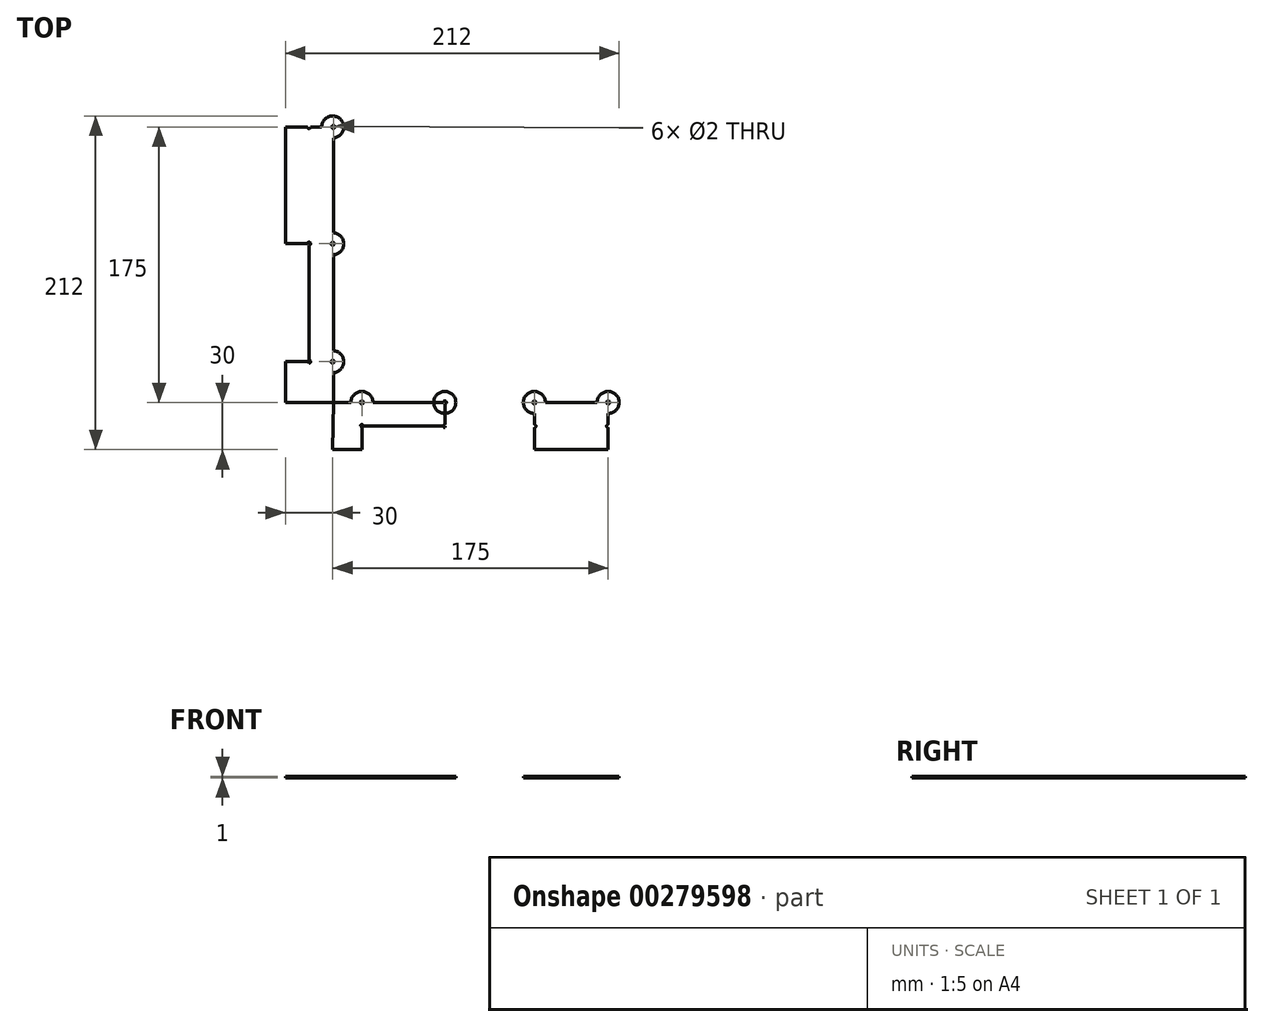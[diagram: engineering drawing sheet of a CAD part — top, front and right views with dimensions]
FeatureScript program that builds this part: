
annotation { "Feature Type Name" : "Feature", "Feature Type Description" : "" }
export const myFeature = defineFeature(function(context is Context, id is Id, definition is map)
    precondition{}
    {
        {
            var Q0;
            Q0=qCreatedBy(makeId("Top.planeOp"),FACE);
            var sketch = newSketch(context, id + "F0", { "sketchPlane" : qUnion([Q0])});
            skLineSegment(sketch, "E0", {"start": v(0, 0) * mm, "end": v(18.55, 0) * mm, "construction": true});
            skCircle(sketch, "E1", {"center": v(18.55, 0) * mm, "radius": 7 * mm});
            skLineSegment(sketch, "E2", {"start": v(0, 0) * mm, "end": v(71.22, 0) * mm, "construction": true});
            skCircle(sketch, "E3", {"center": v(71.22, 0) * mm, "radius": 7 * mm});
            skLineSegment(sketch, "E4", {"start": v(0, 0) * mm, "end": v(128.1, 0) * mm, "construction": true});
            skCircle(sketch, "E5", {"center": v(128.1, 0) * mm, "radius": 7 * mm});
            skLineSegment(sketch, "E6", {"start": v(0, 0) * mm, "end": v(175, 0) * mm, "construction": true});
            skCircle(sketch, "E7", {"center": v(175, 0) * mm, "radius": 7 * mm});
            skLineSegment(sketch, "E8", {"start": v(0, 0) * mm, "end": v(0, 25.9) * mm, "construction": true});
            skLineSegment(sketch, "E9", {"start": v(0, 0) * mm, "end": v(0, 100.8) * mm, "construction": true});
            skLineSegment(sketch, "E10", {"start": v(0, 0) * mm, "end": v(0, 175) * mm, "construction": true});
            skCircle(sketch, "E11", {"center": v(0, 25.9) * mm, "radius": 7 * mm});
            skCircle(sketch, "E12", {"center": v(0, 100.8) * mm, "radius": 7 * mm});
            skCircle(sketch, "E13", {"center": v(0, 175) * mm, "radius": 7 * mm});
            skLineSegment(sketch, "E14.0", {"start": v(0, -15) * mm, "end": v(175, -15) * mm});
            skLineSegment(sketch, "E15.0", {"start": v(0, -30) * mm, "end": v(175, -30) * mm});
            skLineSegment(sketch, "E16.0", {"start": v(0.46, 0) * mm, "end": v(0.46, 175) * mm});
            skLineSegment(sketch, "E17.0", {"start": v(-15, 0) * mm, "end": v(-15, 175) * mm});
            skLineSegment(sketch, "E18.0", {"start": v(-30, 0) * mm, "end": v(-30, 175) * mm});
            skLineSegment(sketch, "E19", {"start": v(18.55, 0) * mm, "end": v(18.55, -30) * mm});
            skLineSegment(sketch, "E20", {"start": v(71.22, 0) * mm, "end": v(71.22, -30) * mm});
            skLineSegment(sketch, "E21", {"start": v(128.1, 0) * mm, "end": v(128.1, -30) * mm});
            skLineSegment(sketch, "E22", {"start": v(175, 0) * mm, "end": v(175, -30) * mm});
            skLineSegment(sketch, "E23", {"start": v(0.46, 175) * mm, "end": v(-30, 175) * mm});
            skLineSegment(sketch, "E24", {"start": v(0, 100.8) * mm, "end": v(-30, 100.8) * mm});
            skPoint(sketch, "E24.endSnap0", {"position": v(-30, 87.5) * mm});
            skLineSegment(sketch, "E25", {"start": v(0, 25.9) * mm, "end": v(-30, 25.9) * mm});
            skCircle(sketch, "E26", {"center": v(-15, 175) * mm, "radius": 1 * mm});
            skCircle(sketch, "E27", {"center": v(-15, 100.8) * mm, "radius": 1 * mm});
            skCircle(sketch, "E28", {"center": v(-15, 25.9) * mm, "radius": 1 * mm});
            skCircle(sketch, "E29", {"center": v(18.55, -15) * mm, "radius": 1 * mm});
            skCircle(sketch, "E30", {"center": v(71.22, -15) * mm, "radius": 1 * mm});
            skCircle(sketch, "E31", {"center": v(128.1, -15) * mm, "radius": 1 * mm});
            skCircle(sketch, "E32", {"center": v(175, -15) * mm, "radius": 1 * mm});
            skLineSegment(sketch, "E33", {"start": v(0.46, 0) * mm, "end": v(0, -30) * mm});
            skLineSegment(sketch, "E34", {"start": v(0.46, 0) * mm, "end": v(-30, 0) * mm});
            skLineSegment(sketch, "E35", {"start": v(0.46, 0) * mm, "end": v(175, 0) * mm});
            skCircle(sketch, "E36", {"center": v(0.46, 175) * mm, "radius": 1 * mm});
            skCircle(sketch, "E37", {"center": v(0, 100.8) * mm, "radius": 1 * mm});
            skCircle(sketch, "E38", {"center": v(0, 25.9) * mm, "radius": 1 * mm});
            skCircle(sketch, "E39", {"center": v(18.55, 0) * mm, "radius": 1 * mm});
            skCircle(sketch, "E40", {"center": v(71.22, 0) * mm, "radius": 1 * mm});
            skCircle(sketch, "E41", {"center": v(128.1, 0) * mm, "radius": 1 * mm});
            skCircle(sketch, "E42", {"center": v(175, 0) * mm, "radius": 1 * mm});
            skSolve(sketch);
        }
        {
            var Q0;
            {var subQ0=sQuery(id+"F0.wireOp",EDGE,"E22");var subQ1=sQuery(id+"F0.wireOp",EDGE,"E7");var subQ2=makeQuery(id+"F0.imprint","INTERSECT",VERTEX,{"derivedFrom":[subQ1,subQ0]});Q0=makeQuery(id+"F0.imprint","IMPRINT",FACE,{"disambiguationData":[TD([[makeQuery(id+"F0.imprint","IMPRINT",EDGE,{"disambiguationData":[TD([[subQ2,-1.0]])],"derivedFrom":subQ1}),1.0]])]});}
            var Q1;
            {var subQ0=sQuery(id+"F0.wireOp",EDGE,"E16.0");var subQ1=sQuery(id+"F0.wireOp",EDGE,"E13");var subQ2=makeQuery(id+"F0.imprint","INTERSECT",VERTEX,{"derivedFrom":[subQ1,subQ0]});Q1=makeQuery(id+"F0.imprint","IMPRINT",FACE,{"disambiguationData":[TD([[makeQuery(id+"F0.imprint","IMPRINT",EDGE,{"disambiguationData":[TD([[subQ2,-1.0]])],"derivedFrom":subQ1}),1.0]])]});}
            var Q2;
            {var subQ0=sQuery(id+"F0.wireOp",EDGE,"E35");var subQ1=sQuery(id+"F0.wireOp",EDGE,"E1");var subQ2=makeQuery(id+"F0.imprint","INTERSECT",VERTEX,{"disambiguationData":[OD(0.0)],"derivedFrom":[subQ1,subQ0]});Q2=makeQuery(id+"F0.imprint","IMPRINT",FACE,{"disambiguationData":[TD([[makeQuery(id+"F0.imprint","IMPRINT",EDGE,{"disambiguationData":[TD([[subQ2,1.0]])],"derivedFrom":subQ1}),1.0]])]});}
            var Q3;
            {var subQ0=sQuery(id+"F0.wireOp",EDGE,"E35");var subQ1=sQuery(id+"F0.wireOp",EDGE,"E3");var subQ2=makeQuery(id+"F0.imprint","INTERSECT",VERTEX,{"disambiguationData":[OD(0.0)],"derivedFrom":[subQ1,subQ0]});Q3=makeQuery(id+"F0.imprint","IMPRINT",FACE,{"disambiguationData":[TD([[makeQuery(id+"F0.imprint","IMPRINT",EDGE,{"disambiguationData":[TD([[subQ2,1.0]])],"derivedFrom":subQ1}),1.0]])]});}
            var Q4;
            {var subQ0=sQuery(id+"F0.wireOp",EDGE,"E35");var subQ1=sQuery(id+"F0.wireOp",EDGE,"E5");var subQ2=makeQuery(id+"F0.imprint","INTERSECT",VERTEX,{"disambiguationData":[OD(0.0)],"derivedFrom":[subQ1,subQ0]});Q4=makeQuery(id+"F0.imprint","IMPRINT",FACE,{"disambiguationData":[TD([[makeQuery(id+"F0.imprint","IMPRINT",EDGE,{"disambiguationData":[TD([[subQ2,1.0]])],"derivedFrom":subQ1}),1.0]])]});}
            var Q5;
            {var subQ0=sQuery(id+"F0.wireOp",EDGE,"E22");var subQ1=sQuery(id+"F0.wireOp",EDGE,"E7");var subQ2=makeQuery(id+"F0.imprint","INTERSECT",VERTEX,{"derivedFrom":[subQ1,subQ0]});Q5=makeQuery(id+"F0.imprint","IMPRINT",FACE,{"disambiguationData":[TD([[makeQuery(id+"F0.imprint","IMPRINT",EDGE,{"disambiguationData":[TD([[subQ2,1.0]])],"derivedFrom":subQ1}),1.0]])]});}
            var Q6;
            {var subQ0=sQuery(id+"F0.wireOp",EDGE,"E16.0");var subQ1=sQuery(id+"F0.wireOp",EDGE,"E11");var subQ2=makeQuery(id+"F0.imprint","INTERSECT",VERTEX,{"disambiguationData":[OD(0.0)],"derivedFrom":[subQ1,subQ0]});Q6=makeQuery(id+"F0.imprint","IMPRINT",FACE,{"disambiguationData":[TD([[makeQuery(id+"F0.imprint","IMPRINT",EDGE,{"disambiguationData":[TD([[subQ2,1.0]])],"derivedFrom":subQ1}),1.0]])]});}
            var Q7;
            {var subQ0=sQuery(id+"F0.wireOp",EDGE,"E16.0");var subQ1=sQuery(id+"F0.wireOp",EDGE,"E12");var subQ2=makeQuery(id+"F0.imprint","INTERSECT",VERTEX,{"disambiguationData":[OD(0.0)],"derivedFrom":[subQ1,subQ0]});Q7=makeQuery(id+"F0.imprint","IMPRINT",FACE,{"disambiguationData":[TD([[makeQuery(id+"F0.imprint","IMPRINT",EDGE,{"disambiguationData":[TD([[subQ2,1.0]])],"derivedFrom":subQ1}),1.0]])]});}
            var Q8;
            {var subQ0=sQuery(id+"F0.wireOp",EDGE,"E16.0");var subQ1=sQuery(id+"F0.wireOp",EDGE,"E13");var subQ2=makeQuery(id+"F0.imprint","INTERSECT",VERTEX,{"derivedFrom":[subQ1,subQ0]});Q8=makeQuery(id+"F0.imprint","IMPRINT",FACE,{"disambiguationData":[TD([[makeQuery(id+"F0.imprint","IMPRINT",EDGE,{"disambiguationData":[TD([[subQ2,1.0]])],"derivedFrom":subQ1}),1.0]])]});}
            var Q9;
            {var subQ1=sQuery(id+"F0.wireOp",EDGE,"E14.0");var subQ7=sQuery(id+"F0.wireOp",EDGE,"E33");var subQ9=makeQuery(id+"F0.imprint","INTERSECT",VERTEX,{"derivedFrom":[subQ1,subQ7]});Q9=makeQuery(id+"F0.imprint","IMPRINT",FACE,{"disambiguationData":[TD([[makeQuery(id+"F0.imprint","IMPRINT",EDGE,{"disambiguationData":[TD([[subQ9,-1.0]])],"derivedFrom":subQ1}),-1.0]])]});}
            var Q10;
            {var subQ5=sQuery(id+"F0.wireOp",EDGE,"E34");var subQ7=sQuery(id+"F0.wireOp",EDGE,"E17.0");var subQ9=makeQuery(id+"F0.imprint","INTERSECT",VERTEX,{"derivedFrom":[subQ7,subQ5]});Q10=makeQuery(id+"F0.imprint","IMPRINT",FACE,{"disambiguationData":[TD([[makeQuery(id+"F0.imprint","IMPRINT",EDGE,{"disambiguationData":[TD([[subQ9,-1.0]])],"derivedFrom":subQ7}),1.0]])]});}
            var Q11;
            {var subQ5=sQuery(id+"F0.wireOp",EDGE,"E35");var subQ6=sQuery(id+"F0.wireOp",EDGE,"E1");var subQ7=makeQuery(id+"F0.imprint","INTERSECT",VERTEX,{"disambiguationData":[OD(0.0)],"derivedFrom":[subQ6,subQ5]});Q11=makeQuery(id+"F0.imprint","IMPRINT",FACE,{"disambiguationData":[TD([[makeQuery(id+"F0.imprint","IMPRINT",EDGE,{"disambiguationData":[TD([[subQ7,-1.0]])],"derivedFrom":subQ6}),-1.0]])]});}
            var Q12;
            {var subQ0=sQuery(id+"F0.wireOp",EDGE,"E35");var subQ1=sQuery(id+"F0.wireOp",EDGE,"E1");var subQ2=makeQuery(id+"F0.imprint","INTERSECT",VERTEX,{"disambiguationData":[OD(0.0)],"derivedFrom":[subQ1,subQ0]});Q12=makeQuery(id+"F0.imprint","IMPRINT",FACE,{"disambiguationData":[TD([[makeQuery(id+"F0.imprint","IMPRINT",EDGE,{"disambiguationData":[TD([[subQ2,-1.0]])],"derivedFrom":subQ1}),1.0]])]});}
            var Q13;
            {var subQ0=sQuery(id+"F0.wireOp",EDGE,"E35");var subQ1=sQuery(id+"F0.wireOp",EDGE,"E1");var subQ2=makeQuery(id+"F0.imprint","INTERSECT",VERTEX,{"disambiguationData":[OD(1.0)],"derivedFrom":[subQ1,subQ0]});Q13=makeQuery(id+"F0.imprint","IMPRINT",FACE,{"disambiguationData":[TD([[makeQuery(id+"F0.imprint","IMPRINT",EDGE,{"disambiguationData":[TD([[subQ2,1.0]])],"derivedFrom":subQ1}),1.0]])]});}
            var Q14;
            {var subQ0=sQuery(id+"F0.wireOp",EDGE,"E35");var subQ1=sQuery(id+"F0.wireOp",EDGE,"E3");var subQ2=makeQuery(id+"F0.imprint","INTERSECT",VERTEX,{"disambiguationData":[OD(0.0)],"derivedFrom":[subQ1,subQ0]});Q14=makeQuery(id+"F0.imprint","IMPRINT",FACE,{"disambiguationData":[TD([[makeQuery(id+"F0.imprint","IMPRINT",EDGE,{"disambiguationData":[TD([[subQ2,-1.0]])],"derivedFrom":subQ1}),1.0]])]});}
            var Q15;
            {var subQ0=sQuery(id+"F0.wireOp",EDGE,"E35");var subQ1=sQuery(id+"F0.wireOp",EDGE,"E3");var subQ2=makeQuery(id+"F0.imprint","INTERSECT",VERTEX,{"disambiguationData":[OD(1.0)],"derivedFrom":[subQ1,subQ0]});Q15=makeQuery(id+"F0.imprint","IMPRINT",FACE,{"disambiguationData":[TD([[makeQuery(id+"F0.imprint","IMPRINT",EDGE,{"disambiguationData":[TD([[subQ2,1.0]])],"derivedFrom":subQ1}),1.0]])]});}
            var Q16;
            {var subQ0=sQuery(id+"F0.wireOp",EDGE,"E35");var subQ1=sQuery(id+"F0.wireOp",EDGE,"E5");var subQ2=makeQuery(id+"F0.imprint","INTERSECT",VERTEX,{"disambiguationData":[OD(0.0)],"derivedFrom":[subQ1,subQ0]});Q16=makeQuery(id+"F0.imprint","IMPRINT",FACE,{"disambiguationData":[TD([[makeQuery(id+"F0.imprint","IMPRINT",EDGE,{"disambiguationData":[TD([[subQ2,-1.0]])],"derivedFrom":subQ1}),1.0]])]});}
            var Q17;
            {var subQ0=sQuery(id+"F0.wireOp",EDGE,"E35");var subQ1=sQuery(id+"F0.wireOp",EDGE,"E5");var subQ2=makeQuery(id+"F0.imprint","INTERSECT",VERTEX,{"disambiguationData":[OD(1.0)],"derivedFrom":[subQ1,subQ0]});Q17=makeQuery(id+"F0.imprint","IMPRINT",FACE,{"disambiguationData":[TD([[makeQuery(id+"F0.imprint","IMPRINT",EDGE,{"disambiguationData":[TD([[subQ2,1.0]])],"derivedFrom":subQ1}),1.0]])]});}
            var Q18;
            {var subQ0=sQuery(id+"F0.wireOp",EDGE,"E16.0");var subQ1=sQuery(id+"F0.wireOp",EDGE,"E11");var subQ2=makeQuery(id+"F0.imprint","INTERSECT",VERTEX,{"disambiguationData":[OD(0.0)],"derivedFrom":[subQ1,subQ0]});Q18=makeQuery(id+"F0.imprint","IMPRINT",FACE,{"disambiguationData":[TD([[makeQuery(id+"F0.imprint","IMPRINT",EDGE,{"disambiguationData":[TD([[subQ2,-1.0]])],"derivedFrom":subQ1}),1.0]])]});}
            var Q19;
            {var subQ1=sQuery(id+"F0.wireOp",EDGE,"E11");var subQ5=sQuery(id+"F0.wireOp",EDGE,"E16.0");var subQ6=makeQuery(id+"F0.imprint","INTERSECT",VERTEX,{"disambiguationData":[OD(1.0)],"derivedFrom":[subQ1,subQ5]});Q19=makeQuery(id+"F0.imprint","IMPRINT",FACE,{"disambiguationData":[TD([[makeQuery(id+"F0.imprint","IMPRINT",EDGE,{"disambiguationData":[TD([[subQ6,1.0]])],"derivedFrom":subQ1}),-1.0]])]});}
            var Q20;
            {var subQ0=sQuery(id+"F0.wireOp",EDGE,"E16.0");var subQ1=sQuery(id+"F0.wireOp",EDGE,"E11");var subQ2=makeQuery(id+"F0.imprint","INTERSECT",VERTEX,{"disambiguationData":[OD(1.0)],"derivedFrom":[subQ1,subQ0]});Q20=makeQuery(id+"F0.imprint","IMPRINT",FACE,{"disambiguationData":[TD([[makeQuery(id+"F0.imprint","IMPRINT",EDGE,{"disambiguationData":[TD([[subQ2,1.0]])],"derivedFrom":subQ1}),1.0]])]});}
            var Q21;
            {var subQ0=sQuery(id+"F0.wireOp",EDGE,"E16.0");var subQ1=sQuery(id+"F0.wireOp",EDGE,"E12");var subQ2=makeQuery(id+"F0.imprint","INTERSECT",VERTEX,{"disambiguationData":[OD(0.0)],"derivedFrom":[subQ1,subQ0]});Q21=makeQuery(id+"F0.imprint","IMPRINT",FACE,{"disambiguationData":[TD([[makeQuery(id+"F0.imprint","IMPRINT",EDGE,{"disambiguationData":[TD([[subQ2,-1.0]])],"derivedFrom":subQ1}),1.0]])]});}
            var Q22;
            {var subQ0=sQuery(id+"F0.wireOp",EDGE,"E16.0");var subQ1=sQuery(id+"F0.wireOp",EDGE,"E12");var subQ2=makeQuery(id+"F0.imprint","INTERSECT",VERTEX,{"disambiguationData":[OD(1.0)],"derivedFrom":[subQ1,subQ0]});Q22=makeQuery(id+"F0.imprint","IMPRINT",FACE,{"disambiguationData":[TD([[makeQuery(id+"F0.imprint","IMPRINT",EDGE,{"disambiguationData":[TD([[subQ2,1.0]])],"derivedFrom":subQ1}),1.0]])]});}
            var Q23;
            {var subQ7=sQuery(id+"F0.wireOp",EDGE,"E31");var subQ9=sQuery(id+"F0.wireOp",EDGE,"E14.0");var subQ10=makeQuery(id+"F0.imprint","INTERSECT",VERTEX,{"disambiguationData":[OD(1.0)],"derivedFrom":[subQ9,subQ7]});Q23=makeQuery(id+"F0.imprint","IMPRINT",FACE,{"disambiguationData":[TD([[makeQuery(id+"F0.imprint","IMPRINT",EDGE,{"disambiguationData":[TD([[subQ10,-1.0]])],"derivedFrom":subQ9}),-1.0]])]});}
            var Q24;
            {var subQ3=sQuery(id+"F0.wireOp",EDGE,"E27");var subQ9=sQuery(id+"F0.wireOp",EDGE,"E17.0");var subQ10=makeQuery(id+"F0.imprint","INTERSECT",VERTEX,{"disambiguationData":[OD(1.0)],"derivedFrom":[subQ9,subQ3]});Q24=makeQuery(id+"F0.imprint","IMPRINT",FACE,{"disambiguationData":[TD([[makeQuery(id+"F0.imprint","IMPRINT",EDGE,{"disambiguationData":[TD([[subQ10,-1.0]])],"derivedFrom":subQ9}),1.0]])]});}
            var Q25;
            {var subQ3=sQuery(id+"F0.wireOp",EDGE,"E29");var subQ9=sQuery(id+"F0.wireOp",EDGE,"E14.0");var subQ10=makeQuery(id+"F0.imprint","INTERSECT",VERTEX,{"disambiguationData":[OD(1.0)],"derivedFrom":[subQ9,subQ3]});Q25=makeQuery(id+"F0.imprint","IMPRINT",FACE,{"disambiguationData":[TD([[makeQuery(id+"F0.imprint","IMPRINT",EDGE,{"disambiguationData":[TD([[subQ10,-1.0]])],"derivedFrom":subQ9}),-1.0]])]});}
            var Q26;
            {var subQ7=sQuery(id+"F0.wireOp",EDGE,"E30");var subQ9=sQuery(id+"F0.wireOp",EDGE,"E14.0");var subQ10=makeQuery(id+"F0.imprint","INTERSECT",VERTEX,{"disambiguationData":[OD(1.0)],"derivedFrom":[subQ9,subQ7]});Q26=makeQuery(id+"F0.imprint","IMPRINT",FACE,{"disambiguationData":[TD([[makeQuery(id+"F0.imprint","IMPRINT",EDGE,{"disambiguationData":[TD([[subQ10,-1.0]])],"derivedFrom":subQ9}),-1.0]])]});}
            var Q27;
            {var subQ3=sQuery(id+"F0.wireOp",EDGE,"E28");var subQ9=sQuery(id+"F0.wireOp",EDGE,"E17.0");var subQ10=makeQuery(id+"F0.imprint","INTERSECT",VERTEX,{"disambiguationData":[OD(1.0)],"derivedFrom":[subQ9,subQ3]});Q27=makeQuery(id+"F0.imprint","IMPRINT",FACE,{"disambiguationData":[TD([[makeQuery(id+"F0.imprint","IMPRINT",EDGE,{"disambiguationData":[TD([[subQ10,-1.0]])],"derivedFrom":subQ9}),1.0]])]});}
            var Q28;
            {var subQ1=sQuery(id+"F0.wireOp",EDGE,"E5");var subQ9=sQuery(id+"F0.wireOp",EDGE,"E35");var subQ10=makeQuery(id+"F0.imprint","INTERSECT",VERTEX,{"disambiguationData":[OD(1.0)],"derivedFrom":[subQ1,subQ9]});Q28=makeQuery(id+"F0.imprint","IMPRINT",FACE,{"disambiguationData":[TD([[makeQuery(id+"F0.imprint","IMPRINT",EDGE,{"disambiguationData":[TD([[subQ10,1.0]])],"derivedFrom":subQ1}),-1.0]])]});}
            var Q29;
            {var subQ9=sQuery(id+"F0.wireOp",EDGE,"E16.0");var subQ11=sQuery(id+"F0.wireOp",EDGE,"E12");var subQ12=makeQuery(id+"F0.imprint","INTERSECT",VERTEX,{"disambiguationData":[OD(0.0)],"derivedFrom":[subQ11,subQ9]});Q29=makeQuery(id+"F0.imprint","IMPRINT",FACE,{"disambiguationData":[TD([[makeQuery(id+"F0.imprint","IMPRINT",EDGE,{"disambiguationData":[TD([[subQ12,-1.0]])],"derivedFrom":subQ11}),-1.0]])]});}
            var Q30;
            {var subQ1=sQuery(id+"F0.wireOp",EDGE,"E1");var subQ9=sQuery(id+"F0.wireOp",EDGE,"E35");var subQ10=makeQuery(id+"F0.imprint","INTERSECT",VERTEX,{"disambiguationData":[OD(1.0)],"derivedFrom":[subQ1,subQ9]});Q30=makeQuery(id+"F0.imprint","IMPRINT",FACE,{"disambiguationData":[TD([[makeQuery(id+"F0.imprint","IMPRINT",EDGE,{"disambiguationData":[TD([[subQ10,1.0]])],"derivedFrom":subQ1}),-1.0]])]});}
            var Q31;
            {var subQ5=sQuery(id+"F0.wireOp",EDGE,"E35");var subQ12=sQuery(id+"F0.wireOp",EDGE,"E3");var subQ15=makeQuery(id+"F0.imprint","INTERSECT",VERTEX,{"disambiguationData":[OD(1.0)],"derivedFrom":[subQ12,subQ5]});Q31=makeQuery(id+"F0.imprint","IMPRINT",FACE,{"disambiguationData":[TD([[makeQuery(id+"F0.imprint","IMPRINT",EDGE,{"disambiguationData":[TD([[subQ15,1.0]])],"derivedFrom":subQ12}),-1.0]])]});}
            var Q32;
            {var subQ5=sQuery(id+"F0.wireOp",EDGE,"E16.0");var subQ6=sQuery(id+"F0.wireOp",EDGE,"E11");var subQ7=makeQuery(id+"F0.imprint","INTERSECT",VERTEX,{"disambiguationData":[OD(0.0)],"derivedFrom":[subQ6,subQ5]});Q32=makeQuery(id+"F0.imprint","IMPRINT",FACE,{"disambiguationData":[TD([[makeQuery(id+"F0.imprint","IMPRINT",EDGE,{"disambiguationData":[TD([[subQ7,-1.0]])],"derivedFrom":subQ6}),-1.0]])]});}
            extrude(context, id + "F1", {"entities" : qUnion([Q0, Q1, Q2, Q3, Q4, Q5, Q6, Q7, Q8, Q9, Q10, Q11, Q12, Q13, Q14, Q15, Q16, Q17, Q18, Q19, Q20, Q21, Q22, Q23, Q24, Q25, Q26, Q27, Q28, Q29, Q30, Q31, Q32]), "depth" : 1 * mm});
        }
    });
